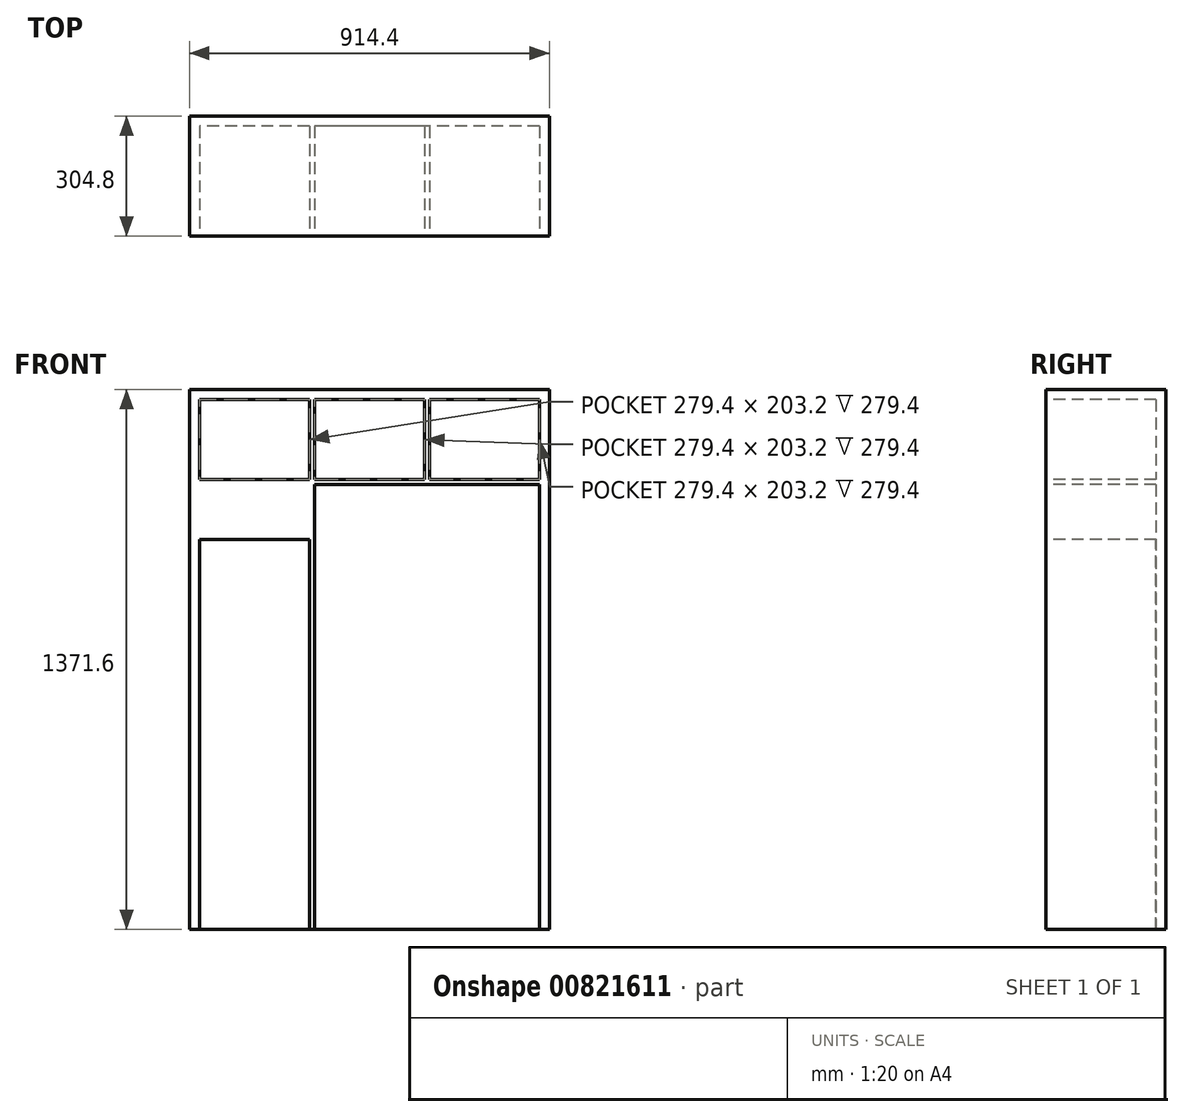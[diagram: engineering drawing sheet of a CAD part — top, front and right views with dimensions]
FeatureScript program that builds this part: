
annotation { "Feature Type Name" : "Feature", "Feature Type Description" : "" }
export const myFeature = defineFeature(function(context is Context, id is Id, definition is map)
    precondition{}
    {
        {
            var Q0;
            Q0=qCreatedBy(makeId("Front.planeOp"),FACE);
            var sketch = newSketch(context, id + "F0", { "sketchPlane" : qUnion([Q0])});
            skLineSegment(sketch, "E0.bottom", {"start": v(0, 0) * mm, "end": v(914.4, 0) * mm});
            skLineSegment(sketch, "E0.top", {"start": v(0, 1371.6) * mm, "end": v(914.4, 1371.6) * mm});
            skLineSegment(sketch, "E0.left", {"start": v(0, 0) * mm, "end": v(0, 1371.6) * mm});
            skLineSegment(sketch, "E0.right", {"start": v(914.4, 0) * mm, "end": v(914.4, 1371.6) * mm});
            skSolve(sketch);
        }
        {
            var Q0;
            Q0 = qSketchRegion(id + "F0", true);
            extrude(context, id + "F1", {"entities" : qUnion([Q0]), "depth" : 304.8 * mm, "offsetDistance" : 25.4 * mm});
        }
        {
            var Q0;
            Q0=makeQuery(id+"F1.opExtrude","CAP_FACE",FACE,{"disambiguationData":[OSD([sQuery(id+"F0.wireOp",EDGE,"E0.bottom"),sQuery(id+"F0.wireOp",EDGE,"E0.top"),sQuery(id+"F0.wireOp",EDGE,"E0.left"),sQuery(id+"F0.wireOp",EDGE,"E0.right")])],"isStart":false});
            var sketch = newSketch(context, id + "F2", { "sketchPlane" : qUnion([Q0])});
            skLineSegment(sketch, "E1.bottom", {"start": v(889, 0) * mm, "end": v(317.5, 0) * mm});
            skLineSegment(sketch, "E1.top", {"start": v(889, 1130.3) * mm, "end": v(317.5, 1130.3) * mm});
            skLineSegment(sketch, "E1.left", {"start": v(889, 0) * mm, "end": v(889, 1130.3) * mm});
            skLineSegment(sketch, "E1.right", {"start": v(317.5, 0) * mm, "end": v(317.5, 1130.3) * mm});
            skLineSegment(sketch, "E2.bottom", {"start": v(25.4, 990.6) * mm, "end": v(304.8, 990.6) * mm});
            skLineSegment(sketch, "E2.top", {"start": v(25.4, 0) * mm, "end": v(304.8, 0) * mm});
            skLineSegment(sketch, "E2.left", {"start": v(25.4, 990.6) * mm, "end": v(25.4, 0) * mm});
            skLineSegment(sketch, "E2.right", {"start": v(304.8, 990.6) * mm, "end": v(304.8, 0) * mm});
            skLineSegment(sketch, "E3.bottom", {"start": v(25.4, 1143) * mm, "end": v(304.8, 1143) * mm});
            skLineSegment(sketch, "E3.top", {"start": v(25.4, 1346.2) * mm, "end": v(304.8, 1346.2) * mm});
            skLineSegment(sketch, "E3.left", {"start": v(25.4, 1143) * mm, "end": v(25.4, 1346.2) * mm});
            skLineSegment(sketch, "E3.right", {"start": v(304.8, 1143) * mm, "end": v(304.8, 1346.2) * mm});
            skLineSegment(sketch, "E4.bottom", {"start": v(317.5, 1143) * mm, "end": v(596.9, 1143) * mm});
            skLineSegment(sketch, "E4.top", {"start": v(317.5, 1346.2) * mm, "end": v(596.9, 1346.2) * mm});
            skLineSegment(sketch, "E4.left", {"start": v(317.5, 1143) * mm, "end": v(317.5, 1346.2) * mm});
            skLineSegment(sketch, "E4.right", {"start": v(596.9, 1143) * mm, "end": v(596.9, 1346.2) * mm});
            skLineSegment(sketch, "E5.bottom", {"start": v(609.6, 1143) * mm, "end": v(889, 1143) * mm});
            skLineSegment(sketch, "E5.top", {"start": v(609.6, 1346.2) * mm, "end": v(889, 1346.2) * mm});
            skLineSegment(sketch, "E5.left", {"start": v(609.6, 1143) * mm, "end": v(609.6, 1346.2) * mm});
            skLineSegment(sketch, "E5.right", {"start": v(889, 1143) * mm, "end": v(889, 1346.2) * mm});
            skSolve(sketch);
        }
        {
            var Q0;
            Q0 = qSketchRegion(id + "F2", true);
            var Q1;
            Q1=makeQuery(id+"F1.opExtrude","CAP_FACE",FACE,{"disambiguationData":[OSD([sQuery(id+"F0.wireOp",EDGE,"E0.bottom"),sQuery(id+"F0.wireOp",EDGE,"E0.top"),sQuery(id+"F0.wireOp",EDGE,"E0.left"),sQuery(id+"F0.wireOp",EDGE,"E0.right")])],"isStart":true});
            extrude(context, id + "F3", {"entities" : qUnion([Q0]), "operationType" : NewBodyOperationType.REMOVE, "endBound" : BoundingType.UP_TO_SURFACE, "oppositeDirection" : true, "depth" : 25.4 * mm, "endBoundEntityFace" : qUnion([Q1]), "hasOffset" : true, "offsetDistance" : 25.4 * mm});
        }
    });
